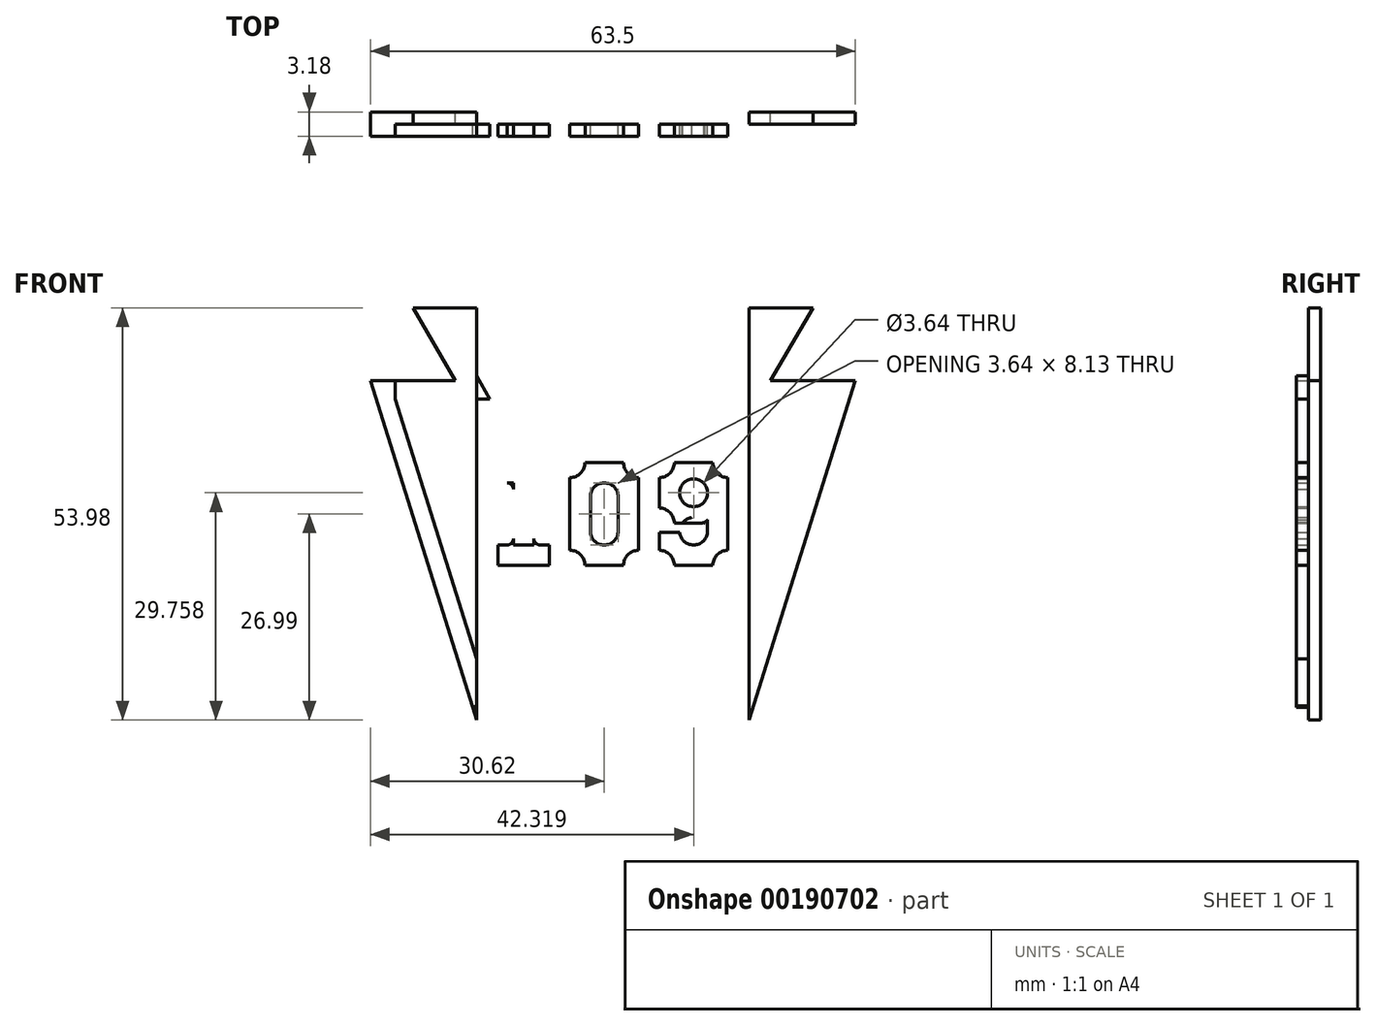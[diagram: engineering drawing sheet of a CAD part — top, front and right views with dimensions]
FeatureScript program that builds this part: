
annotation { "Feature Type Name" : "Feature", "Feature Type Description" : "" }
export const myFeature = defineFeature(function(context is Context, id is Id, definition is map)
    precondition{}
    {
        {
            var Q0;
            Q0=qCreatedBy(makeId("Front.planeOp"),FACE);
            var sketch = newSketch(context, id + "F0", { "sketchPlane" : qUnion([Q0])});
            skLineSegment(sketch, "E0.bottom", {"start": v(-31.75, 26.99) * mm, "end": v(31.75, 26.99) * mm});
            skLineSegment(sketch, "E0.top", {"start": v(-31.75, -26.99) * mm, "end": v(31.75, -26.99) * mm});
            skLineSegment(sketch, "E0.left", {"start": v(-31.75, 26.99) * mm, "end": v(-31.75, -26.99) * mm});
            skLineSegment(sketch, "E0.right", {"start": v(31.75, 26.99) * mm, "end": v(31.75, -26.99) * mm});
            skPoint(sketch, "E1", {"position": v(0, 26.99) * mm});
            skPoint(sketch, "E2", {"position": v(31.75, 0) * mm});
            skLineSegment(sketch, "E3.bottom", {"start": v(-17.86, 26.99) * mm, "end": v(17.86, 26.99) * mm});
            skLineSegment(sketch, "E3.top", {"start": v(-17.86, -26.99) * mm, "end": v(17.86, -26.99) * mm});
            skLineSegment(sketch, "E3.left", {"start": v(-17.86, 26.99) * mm, "end": v(-17.86, -26.99) * mm});
            skLineSegment(sketch, "E3.right", {"start": v(17.86, 26.99) * mm, "end": v(17.86, -26.99) * mm});
            skLineSegment(sketch, "E4", {"start": v(-17.86, -26.99) * mm, "end": v(-31.75, 17.46) * mm});
            skLineSegment(sketch, "E5", {"start": v(17.86, -26.99) * mm, "end": v(31.75, 17.46) * mm});
            skLineSegment(sketch, "E6", {"start": v(-31.75, 17.46) * mm, "end": v(-20.64, 17.46) * mm});
            skLineSegment(sketch, "E7", {"start": v(31.75, 17.46) * mm, "end": v(20.64, 17.46) * mm});
            skPoint(sketch, "E8", {"position": v(-26.2, 17.46) * mm});
            skPoint(sketch, "E9", {"position": v(26.2, 17.46) * mm});
            skLineSegment(sketch, "E10", {"start": v(-20.64, 17.46) * mm, "end": v(-26.2, 26.99) * mm});
            skLineSegment(sketch, "E11", {"start": v(20.64, 17.46) * mm, "end": v(26.2, 26.99) * mm});
            skSolve(sketch);
        }
        {
            var Q0;
            {var subQ0=sQuery(id+"F0.wireOp",EDGE,"E3.right");Q0=makeQuery(id+"F0.imprint","IMPRINT",FACE,{"disambiguationData":[TD([[makeQuery(id+"F0.imprint","IMPRINT",EDGE,{"derivedFrom":subQ0}),1.0]])]});}
            var Q1;
            Q1=makeQuery(id+"F0.imprint","IMPRINT",FACE,{"disambiguationData":[TD([[makeQuery(id+"F0.imprint","IMPRINT",EDGE,{"derivedFrom":sQuery(id+"F0.wireOp",EDGE,"E3.bottom")}),-1.0]])]});
            var Q2;
            {var subQ1=sQuery(id+"F0.wireOp",EDGE,"E3.left");Q2=makeQuery(id+"F0.imprint","IMPRINT",FACE,{"disambiguationData":[TD([[makeQuery(id+"F0.imprint","IMPRINT",EDGE,{"derivedFrom":subQ1}),-1.0]])]});}
            extrude(context, id + "F1", {"entities" : qUnion([Q0, Q1, Q2]), "offsetDistance" : 25.4 * mm, "depth" : 1.59 * mm});
        }
        {
            var Q0;
            Q0=makeQuery(id+"F1.opExtrude","CAP_FACE",FACE,{"disambiguationData":[OSD([sQuery(id+"F0.wireOp",EDGE,"E0.bottom"),sQuery(id+"F0.wireOp",EDGE,"E3.bottom"),sQuery(id+"F0.wireOp",EDGE,"E3.top"),sQuery(id+"F0.wireOp",EDGE,"E4"),sQuery(id+"F0.wireOp",EDGE,"E5"),sQuery(id+"F0.wireOp",EDGE,"E6"),sQuery(id+"F0.wireOp",EDGE,"E7"),sQuery(id+"F0.wireOp",EDGE,"E10"),sQuery(id+"F0.wireOp",EDGE,"E11")])],"isStart":false});
            var sketch = newSketch(context, id + "F2", { "sketchPlane" : qUnion([Q0])});
            skLineSegment(sketch, "E12", {"start": v(-21.66, 24.6) * mm, "end": v(21.66, 24.6) * mm});
            skLineSegment(sketch, "E13", {"start": v(-21.66, 24.6) * mm, "end": v(-16.1, 15.08) * mm});
            skLineSegment(sketch, "E14", {"start": v(-16.1, 15.08) * mm, "end": v(-28.51, 15.08) * mm});
            skLineSegment(sketch, "E15", {"start": v(-28.51, 15.08) * mm, "end": v(-16.1, -24.6) * mm});
            skLineSegment(sketch, "E16", {"start": v(-16.1, -24.6) * mm, "end": v(16.1, -24.6) * mm});
            skLineSegment(sketch, "E17", {"start": v(16.1, -24.6) * mm, "end": v(28.51, 15.08) * mm});
            skLineSegment(sketch, "E18", {"start": v(28.51, 15.08) * mm, "end": v(16.1, 15.08) * mm});
            skLineSegment(sketch, "E19", {"start": v(16.1, 15.08) * mm, "end": v(21.66, 24.6) * mm});
            skPoint(sketch, "E20", {"position": v(0, 24.6) * mm});
            skPoint(sketch, "E21", {"position": v(0, 26.99) * mm});
            skPoint(sketch, "E22", {"position": v(23.42, 22.22) * mm});
            skPoint(sketch, "E23", {"position": v(18.89, 19.84) * mm});
            skPoint(sketch, "E24", {"position": v(-24.8, -4.76) * mm});
            skPoint(sketch, "E25", {"position": v(0, -24.6) * mm});
            skPoint(sketch, "E26", {"position": v(0, -26.99) * mm});
            skLineSegment(sketch, "E27", {"start": v(0, -26.99) * mm, "end": v(0, -24.6) * mm});
            skLineSegment(sketch, "E28", {"start": v(0, 24.6) * mm, "end": v(0, 26.99) * mm});
            skLineSegment(sketch, "E29", {"start": v(-16.1, -24.6) * mm, "end": v(-18.38, -25.32) * mm});
            skLineSegment(sketch, "E30", {"start": v(16.1, -24.6) * mm, "end": v(18.38, -25.32) * mm});
            skLineSegment(sketch, "E31", {"start": v(-28.51, 15.08) * mm, "end": v(-28.51, 17.46) * mm});
            skLineSegment(sketch, "E32", {"start": v(28.51, 15.08) * mm, "end": v(28.51, 17.46) * mm});
            skLineSegment(sketch, "E33.bottom", {"start": v(-15.07, 6.75) * mm, "end": v(-8.33, 6.75) * mm});
            skLineSegment(sketch, "E33.top", {"start": v(-15.07, -6.75) * mm, "end": v(-8.33, -6.75) * mm});
            skLineSegment(sketch, "E33.left", {"start": v(-15.07, 6.75) * mm, "end": v(-15.07, -6.75) * mm});
            skLineSegment(sketch, "E33.right", {"start": v(-8.33, 6.75) * mm, "end": v(-8.33, -6.75) * mm});
            skPoint(sketch, "E34", {"position": v(-15.07, 0) * mm});
            skPoint(sketch, "E35", {"position": v(-11.7, -6.75) * mm});
            skLineSegment(sketch, "E36.bottom", {"start": v(-5.63, 6.75) * mm, "end": v(3.37, 6.75) * mm});
            skLineSegment(sketch, "E36.top", {"start": v(-5.63, -6.75) * mm, "end": v(3.37, -6.75) * mm});
            skLineSegment(sketch, "E36.left", {"start": v(-5.63, 6.75) * mm, "end": v(-5.63, -6.75) * mm});
            skLineSegment(sketch, "E36.right", {"start": v(3.37, 6.75) * mm, "end": v(3.37, -6.75) * mm});
            skLineSegment(sketch, "E37.bottom", {"start": v(6.07, 6.75) * mm, "end": v(15.07, 6.75) * mm});
            skLineSegment(sketch, "E37.top", {"start": v(6.07, -6.75) * mm, "end": v(15.07, -6.75) * mm});
            skLineSegment(sketch, "E37.left", {"start": v(6.07, 6.75) * mm, "end": v(6.07, -6.75) * mm});
            skLineSegment(sketch, "E37.right", {"start": v(15.07, 6.75) * mm, "end": v(15.07, -6.75) * mm});
            skPoint(sketch, "E38", {"position": v(-1.13, -6.75) * mm});
            skPoint(sketch, "E39", {"position": v(10.57, -6.75) * mm});
            skLineSegment(sketch, "E40.bottom", {"start": v(-2.95, 4.06) * mm, "end": v(0.69, 4.06) * mm});
            skLineSegment(sketch, "E40.top", {"start": v(-2.95, -4.06) * mm, "end": v(0.69, -4.06) * mm});
            skLineSegment(sketch, "E40.left", {"start": v(-2.95, 4.06) * mm, "end": v(-2.95, -4.06) * mm});
            skLineSegment(sketch, "E40.right", {"start": v(0.69, 4.06) * mm, "end": v(0.69, -4.06) * mm});
            skPoint(sketch, "E41", {"position": v(-1.13, 4.06) * mm});
            skPoint(sketch, "E42", {"position": v(-1.13, 6.75) * mm});
            skPoint(sketch, "E43", {"position": v(-2.95, 0) * mm});
            skLineSegment(sketch, "E44", {"start": v(-2.95, 4.06) * mm, "end": v(-2.95, 6.75) * mm});
            skLineSegment(sketch, "E45", {"start": v(-2.95, 4.06) * mm, "end": v(-5.63, 4.06) * mm});
            skLineSegment(sketch, "E46.top", {"start": v(-15.07, -4.05) * mm, "end": v(-8.33, -4.05) * mm});
            skLineSegment(sketch, "E46.left", {"start": v(-15.07, -6.75) * mm, "end": v(-15.07, -4.05) * mm});
            skLineSegment(sketch, "E46.right", {"start": v(-8.33, -6.75) * mm, "end": v(-8.33, -4.05) * mm});
            skLineSegment(sketch, "E47.bottom", {"start": v(-15.07, 6.75) * mm, "end": v(-10.35, 6.75) * mm});
            skLineSegment(sketch, "E47.top", {"start": v(-15.07, 4.05) * mm, "end": v(-10.35, 4.05) * mm});
            skLineSegment(sketch, "E47.left", {"start": v(-15.07, 6.75) * mm, "end": v(-15.07, 4.05) * mm});
            skLineSegment(sketch, "E47.right", {"start": v(-10.35, 6.75) * mm, "end": v(-10.35, 4.05) * mm});
            skLineSegment(sketch, "E48.bottom", {"start": v(-10.35, 4.05) * mm, "end": v(-13.04, 4.05) * mm});
            skLineSegment(sketch, "E48.top", {"start": v(-10.35, -4.05) * mm, "end": v(-13.04, -4.05) * mm});
            skLineSegment(sketch, "E48.left", {"start": v(-10.35, 4.05) * mm, "end": v(-10.35, -4.05) * mm});
            skLineSegment(sketch, "E48.right", {"start": v(-13.04, 4.05) * mm, "end": v(-13.04, -4.05) * mm});
            skPoint(sketch, "E49", {"position": v(-11.7, -4.05) * mm});
            skLineSegment(sketch, "E50.bottom", {"start": v(8.75, 4.59) * mm, "end": v(12.39, 4.59) * mm});
            skLineSegment(sketch, "E50.top", {"start": v(8.75, -4.06) * mm, "end": v(12.39, -4.06) * mm});
            skLineSegment(sketch, "E50.left", {"start": v(8.75, 4.59) * mm, "end": v(8.75, -4.06) * mm});
            skLineSegment(sketch, "E50.right", {"start": v(12.39, 4.59) * mm, "end": v(12.39, -4.06) * mm});
            skPoint(sketch, "E51", {"position": v(10.57, -4.06) * mm});
            skCircle(sketch, "E52", {"center": v(10.57, 2.77) * mm, "radius": 1.82 * mm});
            skLineSegment(sketch, "E53", {"start": v(6.07, -2.44) * mm, "end": v(8.75, -2.44) * mm});
            skCircle(sketch, "E54", {"center": v(6.07, 6.75) * mm, "radius": 1.98 * mm});
            skCircle(sketch, "E55", {"center": v(15.07, 6.75) * mm, "radius": 1.98 * mm});
            skCircle(sketch, "E56", {"center": v(15.07, -6.75) * mm, "radius": 1.98 * mm});
            skCircle(sketch, "E57", {"center": v(6.07, -6.75) * mm, "radius": 1.98 * mm});
            skCircle(sketch, "E58", {"center": v(-5.63, -6.75) * mm, "radius": 1.98 * mm});
            skCircle(sketch, "E59", {"center": v(3.37, -6.75) * mm, "radius": 1.98 * mm});
            skCircle(sketch, "E60", {"center": v(3.37, 6.75) * mm, "radius": 1.98 * mm});
            skCircle(sketch, "E61", {"center": v(-5.63, 6.75) * mm, "radius": 1.98 * mm});
            skCircle(sketch, "E62", {"center": v(-13.84, 3.26) * mm, "radius": 0.8 * mm});
            skCircle(sketch, "E63", {"center": v(-13.84, -3.26) * mm, "radius": 0.8 * mm});
            skCircle(sketch, "E64", {"center": v(-9.56, -3.26) * mm, "radius": 0.8 * mm});
            skCircle(sketch, "E65", {"center": v(-1.15, 2.26) * mm, "radius": 1.8 * mm});
            skCircle(sketch, "E66", {"center": v(-1.11, 2.26) * mm, "radius": 1.8 * mm});
            skCircle(sketch, "E67", {"center": v(-1.15, -2.26) * mm, "radius": 1.8 * mm});
            skCircle(sketch, "E68", {"center": v(-1.11, -2.26) * mm, "radius": 1.8 * mm});
            skLineSegment(sketch, "E69", {"start": v(6.07, -1.21) * mm, "end": v(15.07, -1.21) * mm});
            skLineSegment(sketch, "E70", {"start": v(10.57, 4.59) * mm, "end": v(10.57, 6.75) * mm});
            skLineSegment(sketch, "E71", {"start": v(10.57, 0.95) * mm, "end": v(10.57, -1.21) * mm});
            skCircle(sketch, "E72", {"center": v(6.07, -1.21) * mm, "radius": 1.98 * mm});
            skCircle(sketch, "E73", {"center": v(11.48, -0.02) * mm, "radius": 1.2 * mm});
            skCircle(sketch, "E74", {"center": v(10.55, -2.26) * mm, "radius": 1.8 * mm});
            skCircle(sketch, "E75", {"center": v(10.59, -2.26) * mm, "radius": 1.8 * mm});
            skLineSegment(sketch, "E76", {"start": v(-15.07, -6.75) * mm, "end": v(-21.69, -6.75) * mm});
            skLineSegment(sketch, "E77", {"start": v(15.07, -6.75) * mm, "end": v(21.69, -6.75) * mm});
            skLineSegment(sketch, "E78", {"start": v(8.75, -2.44) * mm, "end": v(8.76, -2.44) * mm});
            skSolve(sketch);
        }
        {
            var Q0;
            Q0=makeQuery(id+"F2.imprint","IMPRINT",FACE,{"disambiguationData":[TD([[makeQuery(id+"F2.imprint","IMPRINT",EDGE,{"derivedFrom":sQuery(id+"F2.wireOp",EDGE,"E15")}),-1.0]])]});
            var Q1;
            {var subQ1=sQuery(id+"F2.wireOp",EDGE,"E13");Q1=makeQuery(id+"F2.imprint","IMPRINT",FACE,{"disambiguationData":[TD([[makeQuery(id+"F2.imprint","IMPRINT",EDGE,{"derivedFrom":subQ1}),-1.0]])]});}
            var Q2;
            Q2=makeQuery(id+"F2.imprint","IMPRINT",FACE,{"disambiguationData":[TD([[makeQuery(id+"F2.imprint","IMPRINT",EDGE,{"derivedFrom":sQuery(id+"F2.wireOp",EDGE,"E18")}),-1.0]])]});
            var Q3;
            Q3=makeQuery(id+"F2.imprint","IMPRINT",FACE,{"disambiguationData":[TD([[makeQuery(id+"F2.imprint","IMPRINT",EDGE,{"derivedFrom":sQuery(id+"F2.wireOp",EDGE,"E17")}),-1.0]])]});
            var Q4;
            {var subQ3=sQuery(id+"F2.wireOp",EDGE,"E27");Q4=makeQuery(id+"F2.imprint","IMPRINT",FACE,{"disambiguationData":[TD([[makeQuery(id+"F2.imprint","IMPRINT",EDGE,{"derivedFrom":subQ3}),-1.0]])]});}
            var Q5;
            {var subQ3=sQuery(id+"F2.wireOp",EDGE,"E27");Q5=makeQuery(id+"F2.imprint","IMPRINT",FACE,{"disambiguationData":[TD([[makeQuery(id+"F2.imprint","IMPRINT",EDGE,{"derivedFrom":subQ3}),1.0]])]});}
            var Q6;
            Q6=makeQuery(id+"F2.imprint","IMPRINT",FACE,{"disambiguationData":[TD([[makeQuery(id+"F2.imprint","IMPRINT",EDGE,{"derivedFrom":sQuery(id+"F2.wireOp",EDGE,"E47.bottom")}),-1.0]])]});
            var Q7;
            {var subQ1=sQuery(id+"F2.wireOp",EDGE,"E47.top");var subQ3=sQuery(id+"F2.wireOp",EDGE,"E62");var subQ4=makeQuery(id+"F2.imprint","INTERSECT",VERTEX,{"derivedFrom":[subQ1,subQ3]});Q7=makeQuery(id+"F2.imprint","IMPRINT",FACE,{"disambiguationData":[TD([[makeQuery(id+"F2.imprint","IMPRINT",EDGE,{"disambiguationData":[TD([[subQ4,1.0]])],"derivedFrom":subQ3}),-1.0]])]});}
            var Q8;
            {var subQ4=sQuery(id+"F2.wireOp",EDGE,"E48.bottom");Q8=makeQuery(id+"F2.imprint","IMPRINT",FACE,{"disambiguationData":[TD([[makeQuery(id+"F2.imprint","IMPRINT",EDGE,{"derivedFrom":subQ4}),1.0]])]});}
            var Q9;
            {var subQ1=sQuery(id+"F2.wireOp",EDGE,"E46.top");var subQ3=sQuery(id+"F2.wireOp",EDGE,"E63");var subQ4=makeQuery(id+"F2.imprint","INTERSECT",VERTEX,{"derivedFrom":[subQ1,subQ3]});Q9=makeQuery(id+"F2.imprint","IMPRINT",FACE,{"disambiguationData":[TD([[makeQuery(id+"F2.imprint","IMPRINT",EDGE,{"disambiguationData":[TD([[subQ4,-1.0]])],"derivedFrom":subQ3}),-1.0]])]});}
            var Q10;
            {var subQ1=sQuery(id+"F2.wireOp",EDGE,"E46.top");var subQ3=sQuery(id+"F2.wireOp",EDGE,"E64");var subQ4=makeQuery(id+"F2.imprint","INTERSECT",VERTEX,{"derivedFrom":[subQ1,subQ3]});Q10=makeQuery(id+"F2.imprint","IMPRINT",FACE,{"disambiguationData":[TD([[makeQuery(id+"F2.imprint","IMPRINT",EDGE,{"disambiguationData":[TD([[subQ4,1.0]])],"derivedFrom":subQ3}),-1.0]])]});}
            var Q11;
            Q11=makeQuery(id+"F2.imprint","IMPRINT",FACE,{"disambiguationData":[TD([[makeQuery(id+"F2.imprint","IMPRINT",EDGE,{"derivedFrom":sQuery(id+"F2.wireOp",EDGE,"E33.top")}),1.0]])]});
            var Q12;
            {var subQ6=sQuery(id+"F2.wireOp",EDGE,"E44");Q12=makeQuery(id+"F2.imprint","IMPRINT",FACE,{"disambiguationData":[TD([[makeQuery(id+"F2.imprint","IMPRINT",EDGE,{"derivedFrom":subQ6}),1.0]])]});}
            var Q13;
            {var subQ15=sQuery(id+"F2.wireOp",EDGE,"E44");Q13=makeQuery(id+"F2.imprint","IMPRINT",FACE,{"disambiguationData":[TD([[makeQuery(id+"F2.imprint","IMPRINT",EDGE,{"derivedFrom":subQ15}),-1.0]])]});}
            var Q14;
            {var subQ1=sQuery(id+"F2.wireOp",EDGE,"E40.bottom");var subQ3=sQuery(id+"F2.wireOp",EDGE,"E65");var subQ4=makeQuery(id+"F2.imprint","INTERSECT",VERTEX,{"derivedFrom":[subQ1,subQ3]});Q14=makeQuery(id+"F2.imprint","IMPRINT",FACE,{"disambiguationData":[TD([[makeQuery(id+"F2.imprint","IMPRINT",EDGE,{"disambiguationData":[TD([[subQ4,-1.0]])],"derivedFrom":subQ3}),-1.0]])]});}
            var Q15;
            {var subQ0=sQuery(id+"F2.wireOp",EDGE,"E40.right");var subQ1=sQuery(id+"F2.wireOp",EDGE,"E40.bottom");var subQ2=makeQuery(id+"F2.imprint","INTERSECT",VERTEX,{"derivedFrom":[subQ1,subQ0]});Q15=makeQuery(id+"F2.imprint","IMPRINT",FACE,{"disambiguationData":[TD([[makeQuery(id+"F2.imprint","IMPRINT",EDGE,{"disambiguationData":[TD([[subQ2,1.0]])],"derivedFrom":subQ1}),-1.0]])]});}
            var Q16;
            {var subQ0=sQuery(id+"F2.wireOp",EDGE,"E40.right");var subQ1=sQuery(id+"F2.wireOp",EDGE,"E40.top");var subQ2=makeQuery(id+"F2.imprint","INTERSECT",VERTEX,{"derivedFrom":[subQ1,subQ0]});Q16=makeQuery(id+"F2.imprint","IMPRINT",FACE,{"disambiguationData":[TD([[makeQuery(id+"F2.imprint","IMPRINT",EDGE,{"disambiguationData":[TD([[subQ2,1.0]])],"derivedFrom":subQ1}),1.0]])]});}
            var Q17;
            {var subQ0=sQuery(id+"F2.wireOp",EDGE,"E40.left");var subQ1=sQuery(id+"F2.wireOp",EDGE,"E40.top");var subQ2=makeQuery(id+"F2.imprint","INTERSECT",VERTEX,{"derivedFrom":[subQ1,subQ0]});Q17=makeQuery(id+"F2.imprint","IMPRINT",FACE,{"disambiguationData":[TD([[makeQuery(id+"F2.imprint","IMPRINT",EDGE,{"disambiguationData":[TD([[subQ2,-1.0]])],"derivedFrom":subQ1}),1.0]])]});}
            var Q18;
            {var subQ5=sQuery(id+"F2.wireOp",EDGE,"E50.top");Q18=makeQuery(id+"F2.imprint","IMPRINT",FACE,{"disambiguationData":[TD([[makeQuery(id+"F2.imprint","IMPRINT",EDGE,{"derivedFrom":subQ5}),-1.0]])]});}
            var Q19;
            {var subQ0=sQuery(id+"F2.wireOp",EDGE,"E53");var subQ1=sQuery(id+"F2.wireOp",EDGE,"E37.left");var subQ2=makeQuery(id+"F2.imprint","INTERSECT",VERTEX,{"derivedFrom":[subQ1,subQ0]});Q19=makeQuery(id+"F2.imprint","IMPRINT",FACE,{"disambiguationData":[TD([[makeQuery(id+"F2.imprint","IMPRINT",EDGE,{"disambiguationData":[TD([[subQ2,-1.0]])],"derivedFrom":subQ1}),1.0]])]});}
            var Q20;
            {var subQ0=sQuery(id+"F2.wireOp",EDGE,"E54");var subQ3=sQuery(id+"F2.wireOp",EDGE,"E37.left");var subQ4=makeQuery(id+"F2.imprint","INTERSECT",VERTEX,{"derivedFrom":[subQ3,subQ0]});Q20=makeQuery(id+"F2.imprint","IMPRINT",FACE,{"disambiguationData":[TD([[makeQuery(id+"F2.imprint","IMPRINT",EDGE,{"disambiguationData":[TD([[subQ4,-1.0]])],"derivedFrom":subQ3}),1.0]])]});}
            var Q21;
            {var subQ5=sQuery(id+"F2.wireOp",EDGE,"E70");Q21=makeQuery(id+"F2.imprint","IMPRINT",FACE,{"disambiguationData":[TD([[makeQuery(id+"F2.imprint","IMPRINT",EDGE,{"derivedFrom":subQ5}),1.0]])]});}
            var Q22;
            {var subQ0=sQuery(id+"F2.wireOp",EDGE,"E70");Q22=makeQuery(id+"F2.imprint","IMPRINT",FACE,{"disambiguationData":[TD([[makeQuery(id+"F2.imprint","IMPRINT",EDGE,{"derivedFrom":subQ0}),-1.0]])]});}
            var Q23;
            {var subQ3=sQuery(id+"F2.wireOp",EDGE,"E37.right");var subQ9=sQuery(id+"F2.wireOp",EDGE,"E69");var subQ11=makeQuery(id+"F2.imprint","INTERSECT",VERTEX,{"derivedFrom":[subQ3,subQ9]});Q23=makeQuery(id+"F2.imprint","IMPRINT",FACE,{"disambiguationData":[TD([[makeQuery(id+"F2.imprint","IMPRINT",EDGE,{"disambiguationData":[TD([[subQ11,1.0]])],"derivedFrom":subQ3}),-1.0]])]});}
            var Q24;
            {var subQ0=sQuery(id+"F2.wireOp",EDGE,"E50.left");var subQ1=sQuery(id+"F2.wireOp",EDGE,"E50.bottom");var subQ2=makeQuery(id+"F2.imprint","INTERSECT",VERTEX,{"derivedFrom":[subQ1,subQ0]});Q24=makeQuery(id+"F2.imprint","IMPRINT",FACE,{"disambiguationData":[TD([[makeQuery(id+"F2.imprint","IMPRINT",EDGE,{"disambiguationData":[TD([[subQ2,-1.0]])],"derivedFrom":subQ0}),1.0]])]});}
            var Q25;
            {var subQ0=sQuery(id+"F2.wireOp",EDGE,"E50.right");var subQ1=sQuery(id+"F2.wireOp",EDGE,"E50.bottom");var subQ2=makeQuery(id+"F2.imprint","INTERSECT",VERTEX,{"derivedFrom":[subQ1,subQ0]});Q25=makeQuery(id+"F2.imprint","IMPRINT",FACE,{"disambiguationData":[TD([[makeQuery(id+"F2.imprint","IMPRINT",EDGE,{"disambiguationData":[TD([[subQ2,-1.0]])],"derivedFrom":subQ0}),-1.0]])]});}
            var Q26;
            {var subQ0=sQuery(id+"F2.wireOp",EDGE,"E50.left");var subQ1=sQuery(id+"F2.wireOp",EDGE,"E50.top");var subQ2=makeQuery(id+"F2.imprint","INTERSECT",VERTEX,{"derivedFrom":[subQ1,subQ0]});Q26=makeQuery(id+"F2.imprint","IMPRINT",FACE,{"disambiguationData":[TD([[makeQuery(id+"F2.imprint","IMPRINT",EDGE,{"disambiguationData":[TD([[subQ2,-1.0]])],"derivedFrom":subQ1}),1.0]])]});}
            var Q27;
            {var subQ0=sQuery(id+"F2.wireOp",EDGE,"E50.right");var subQ1=sQuery(id+"F2.wireOp",EDGE,"E50.top");var subQ2=makeQuery(id+"F2.imprint","INTERSECT",VERTEX,{"derivedFrom":[subQ1,subQ0]});Q27=makeQuery(id+"F2.imprint","IMPRINT",FACE,{"disambiguationData":[TD([[makeQuery(id+"F2.imprint","IMPRINT",EDGE,{"disambiguationData":[TD([[subQ2,1.0]])],"derivedFrom":subQ1}),1.0]])]});}
            var Q28;
            {var subQ0=sQuery(id+"F2.wireOp",EDGE,"E73");var subQ1=sQuery(id+"F2.wireOp",EDGE,"E50.right");var subQ2=makeQuery(id+"F2.imprint","INTERSECT",VERTEX,{"disambiguationData":[OD(0.0)],"derivedFrom":[subQ1,subQ0]});Q28=makeQuery(id+"F2.imprint","IMPRINT",FACE,{"disambiguationData":[TD([[makeQuery(id+"F2.imprint","IMPRINT",EDGE,{"disambiguationData":[TD([[subQ2,-1.0]])],"derivedFrom":subQ1}),1.0]])]});}
            var Q29;
            {var subQ0=sQuery(id+"F2.wireOp",EDGE,"E52");var subQ1=sQuery(id+"F2.wireOp",EDGE,"E50.right");var subQ2=makeQuery(id+"F2.imprint","INTERSECT",VERTEX,{"derivedFrom":[subQ1,subQ0]});Q29=makeQuery(id+"F2.imprint","IMPRINT",FACE,{"disambiguationData":[TD([[makeQuery(id+"F2.imprint","IMPRINT",EDGE,{"disambiguationData":[TD([[subQ2,-1.0]])],"derivedFrom":subQ1}),-1.0]])]});}
            var Q30;
            {var subQ3=sQuery(id+"F2.wireOp",EDGE,"E73");var subQ6=sQuery(id+"F2.wireOp",EDGE,"E50.right");var subQ7=makeQuery(id+"F2.imprint","INTERSECT",VERTEX,{"disambiguationData":[OD(0.0)],"derivedFrom":[subQ6,subQ3]});Q30=makeQuery(id+"F2.imprint","IMPRINT",FACE,{"disambiguationData":[TD([[makeQuery(id+"F2.imprint","IMPRINT",EDGE,{"disambiguationData":[TD([[subQ7,-1.0]])],"derivedFrom":subQ6}),-1.0]])]});}
            var Q31;
            {var subQ5=sQuery(id+"F2.wireOp",EDGE,"E52");var subQ6=sQuery(id+"F2.wireOp",EDGE,"E50.left");var subQ7=makeQuery(id+"F2.imprint","INTERSECT",VERTEX,{"derivedFrom":[subQ6,subQ5]});Q31=makeQuery(id+"F2.imprint","IMPRINT",FACE,{"disambiguationData":[TD([[makeQuery(id+"F2.imprint","IMPRINT",EDGE,{"disambiguationData":[TD([[subQ7,-1.0]])],"derivedFrom":subQ6}),1.0]])]});}
            var Q32;
            {var subQ0=sQuery(id+"F2.wireOp",EDGE,"E71");var subQ1=sQuery(id+"F2.wireOp",EDGE,"E52");var subQ2=makeQuery(id+"F2.imprint","INTERSECT",VERTEX,{"derivedFrom":[subQ1,subQ0]});Q32=makeQuery(id+"F2.imprint","IMPRINT",FACE,{"disambiguationData":[TD([[makeQuery(id+"F2.imprint","IMPRINT",EDGE,{"disambiguationData":[TD([[subQ2,1.0]])],"derivedFrom":subQ1}),-1.0]])]});}
            var Q33;
            {var subQ0=sQuery(id+"F2.wireOp",EDGE,"E71");var subQ1=sQuery(id+"F2.wireOp",EDGE,"E69");var subQ2=makeQuery(id+"F2.imprint","INTERSECT",VERTEX,{"derivedFrom":[subQ1,subQ0]});Q33=makeQuery(id+"F2.imprint","IMPRINT",FACE,{"disambiguationData":[TD([[makeQuery(id+"F2.imprint","IMPRINT",EDGE,{"disambiguationData":[TD([[subQ2,-1.0]])],"derivedFrom":subQ1}),1.0]])]});}
            var Q34;
            {var subQ0=sQuery(id+"F2.wireOp",EDGE,"E71");var subQ1=sQuery(id+"F2.wireOp",EDGE,"E52");var subQ2=makeQuery(id+"F2.imprint","INTERSECT",VERTEX,{"derivedFrom":[subQ1,subQ0]});Q34=makeQuery(id+"F2.imprint","IMPRINT",FACE,{"disambiguationData":[TD([[makeQuery(id+"F2.imprint","IMPRINT",EDGE,{"disambiguationData":[TD([[subQ2,-1.0]])],"derivedFrom":subQ1}),-1.0]])]});}
            var Q35;
            {var subQ0=sQuery(id+"F2.wireOp",EDGE,"E73");var subQ1=sQuery(id+"F2.wireOp",EDGE,"E71");var subQ2=makeQuery(id+"F2.imprint","INTERSECT",VERTEX,{"disambiguationData":[OD(0.0)],"derivedFrom":[subQ1,subQ0]});Q35=makeQuery(id+"F2.imprint","IMPRINT",FACE,{"disambiguationData":[TD([[makeQuery(id+"F2.imprint","IMPRINT",EDGE,{"disambiguationData":[TD([[subQ2,-1.0]])],"derivedFrom":subQ1}),-1.0]])]});}
            var Q36;
            {var subQ0=sQuery(id+"F2.wireOp",EDGE,"E71");var subQ1=sQuery(id+"F2.wireOp",EDGE,"E69");var subQ2=makeQuery(id+"F2.imprint","INTERSECT",VERTEX,{"derivedFrom":[subQ1,subQ0]});Q36=makeQuery(id+"F2.imprint","IMPRINT",FACE,{"disambiguationData":[TD([[makeQuery(id+"F2.imprint","IMPRINT",EDGE,{"disambiguationData":[TD([[subQ2,1.0]])],"derivedFrom":subQ1}),1.0]])]});}
            var Q37;
            {var subQ0=sQuery(id+"F2.wireOp",EDGE,"E73");var subQ6=makeQuery(id+"F2.imprint","INTERSECT",VERTEX,{"derivedFrom":[sQuery(id+"F2.wireOp",EDGE,"E69"),subQ0]});Q37=makeQuery(id+"F2.imprint","IMPRINT",FACE,{"disambiguationData":[TD([[makeQuery(id+"F2.imprint","IMPRINT",EDGE,{"disambiguationData":[TD([[subQ6,1.0]])],"derivedFrom":subQ0}),1.0]])]});}
            var Q38;
            {var subQ0=sQuery(id+"F2.wireOp",EDGE,"E73");var subQ1=sQuery(id+"F2.wireOp",EDGE,"E71");var subQ2=makeQuery(id+"F2.imprint","INTERSECT",VERTEX,{"disambiguationData":[OD(1.0)],"derivedFrom":[subQ1,subQ0]});Q38=makeQuery(id+"F2.imprint","IMPRINT",FACE,{"disambiguationData":[TD([[makeQuery(id+"F2.imprint","IMPRINT",EDGE,{"disambiguationData":[TD([[subQ2,1.0]])],"derivedFrom":subQ0}),1.0]])]});}
            var Q39;
            {var subQ0=sQuery(id+"F2.wireOp",EDGE,"E74");var subQ1=sQuery(id+"F2.wireOp",EDGE,"E69");var subQ2=makeQuery(id+"F2.imprint","INTERSECT",VERTEX,{"disambiguationData":[OD(0.0)],"derivedFrom":[subQ1,subQ0]});Q39=makeQuery(id+"F2.imprint","IMPRINT",FACE,{"disambiguationData":[TD([[makeQuery(id+"F2.imprint","IMPRINT",EDGE,{"disambiguationData":[TD([[subQ2,-1.0]])],"derivedFrom":subQ1}),1.0]])]});}
            var Q40;
            {var subQ0=sQuery(id+"F2.wireOp",EDGE,"E74");var subQ1=sQuery(id+"F2.wireOp",EDGE,"E73");var subQ2=makeQuery(id+"F2.imprint","INTERSECT",VERTEX,{"disambiguationData":[OD(1.0)],"derivedFrom":[subQ1,subQ0]});Q40=makeQuery(id+"F2.imprint","IMPRINT",FACE,{"disambiguationData":[TD([[makeQuery(id+"F2.imprint","IMPRINT",EDGE,{"disambiguationData":[TD([[subQ2,-1.0]])],"derivedFrom":subQ1}),1.0]])]});}
            var Q41;
            {var subQ0=sQuery(id+"F2.wireOp",EDGE,"E74");var subQ1=sQuery(id+"F2.wireOp",EDGE,"E73");var subQ2=makeQuery(id+"F2.imprint","INTERSECT",VERTEX,{"disambiguationData":[OD(0.0)],"derivedFrom":[subQ1,subQ0]});Q41=makeQuery(id+"F2.imprint","IMPRINT",FACE,{"disambiguationData":[TD([[makeQuery(id+"F2.imprint","IMPRINT",EDGE,{"disambiguationData":[TD([[subQ2,-1.0]])],"derivedFrom":subQ1}),1.0]])]});}
            extrude(context, id + "F3", {"entities" : qUnion([Q0, Q1, Q2, Q3, Q4, Q5, Q6, Q7, Q8, Q9, Q10, Q11, Q12, Q13, Q14, Q15, Q16, Q17, Q18, Q19, Q20, Q21, Q22, Q23, Q24, Q25, Q26, Q27, Q28, Q29, Q30, Q31, Q32, Q33, Q34, Q35, Q36, Q37, Q38, Q39, Q40, Q41]), "operationType" : NewBodyOperationType.ADD, "offsetDistance" : 25.4 * mm, "depth" : 1.59 * mm});
        }
    });
